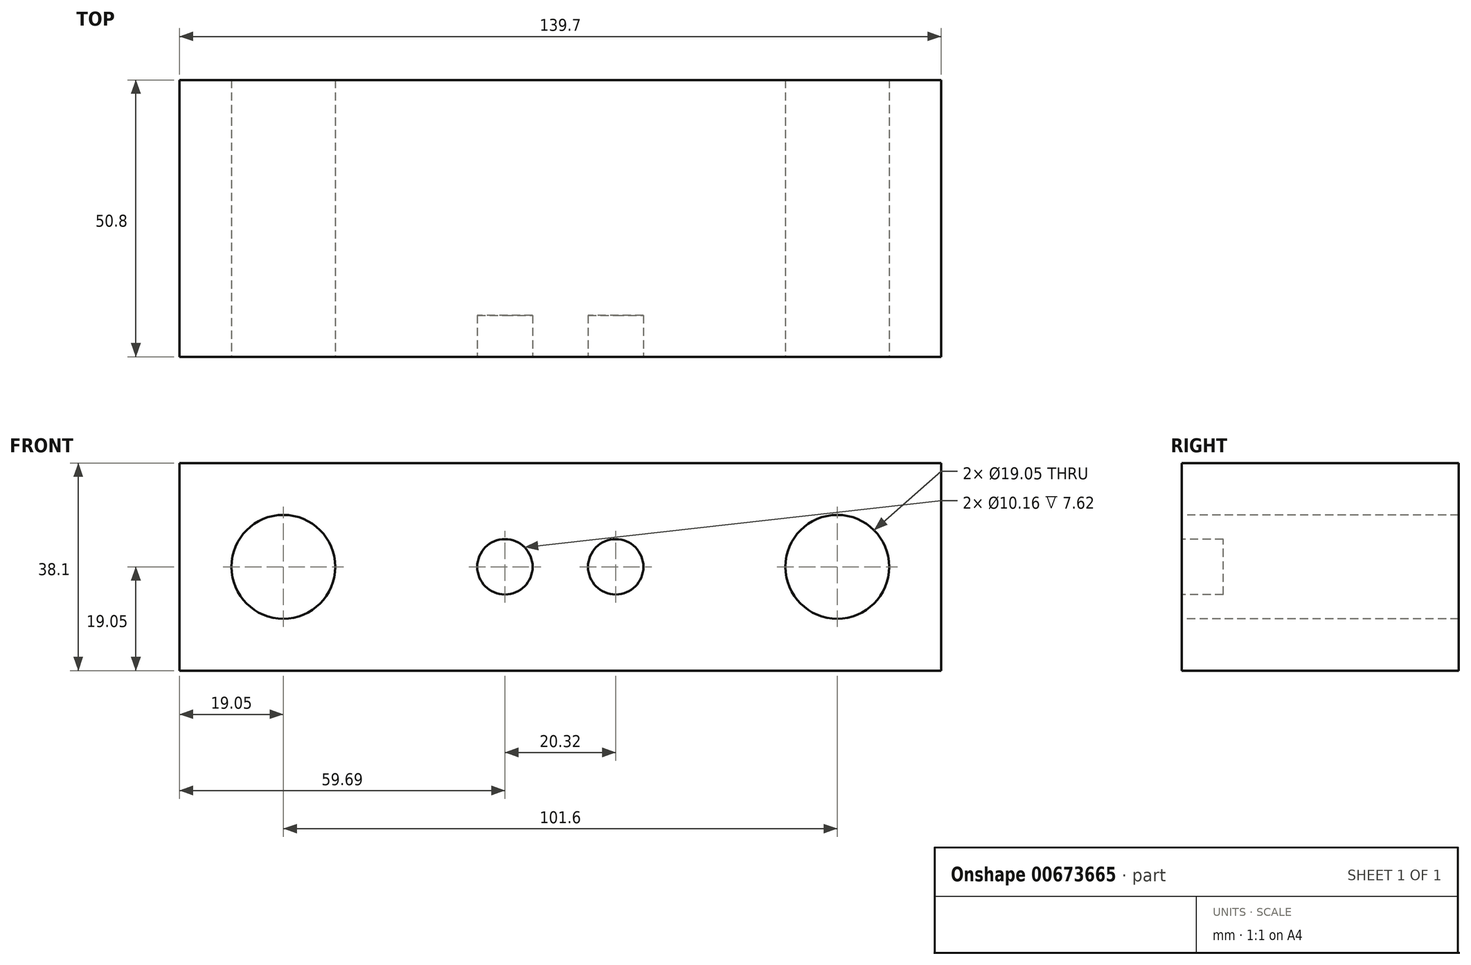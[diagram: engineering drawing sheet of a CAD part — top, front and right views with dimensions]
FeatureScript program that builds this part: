
annotation { "Feature Type Name" : "Feature", "Feature Type Description" : "" }
export const myFeature = defineFeature(function(context is Context, id is Id, definition is map)
    precondition{}
    {
        {
            var Q0;
            Q0=qCreatedBy(makeId("Front.planeOp"),FACE);
            var sketch = newSketch(context, id + "F0", { "sketchPlane" : qUnion([Q0])});
            skLineSegment(sketch, "E0.bottom", {"start": v(69.85, -19.05) * mm, "end": v(-69.85, -19.05) * mm});
            skLineSegment(sketch, "E0.top", {"start": v(69.85, 19.05) * mm, "end": v(-69.85, 19.05) * mm});
            skLineSegment(sketch, "E0.left", {"start": v(69.85, -19.05) * mm, "end": v(69.85, 19.05) * mm});
            skLineSegment(sketch, "E0.right", {"start": v(-69.85, -19.05) * mm, "end": v(-69.85, 19.05) * mm});
            skPoint(sketch, "E0.middle", {"position": v(0, 0) * mm});
            skSolve(sketch);
        }
        {
            var Q0;
            Q0=makeQuery(id+"F0.imprint","IMPRINT",FACE,{"disambiguationData":[TD([[makeQuery(id+"F0.imprint","IMPRINT",EDGE,{"derivedFrom":sQuery(id+"F0.wireOp",EDGE,"E0.bottom")}),-1.0]])]});
            extrude(context, id + "F1", {"entities" : qUnion([Q0]), "endBound" : BoundingType.SYMMETRIC, "depth" : 50.8 * mm, "offsetDistance" : 25.4 * mm});
        }
        {
            var Q0;
            Q0=makeQuery(id+"F1.opExtrude","CAP_FACE",FACE,{"disambiguationData":[OSD([sQuery(id+"F0.wireOp",EDGE,"E0.bottom"),sQuery(id+"F0.wireOp",EDGE,"E0.top"),sQuery(id+"F0.wireOp",EDGE,"E0.left"),sQuery(id+"F0.wireOp",EDGE,"E0.right")])],"isStart":false});
            var sketch = newSketch(context, id + "F2", { "sketchPlane" : qUnion([Q0])});
            skCircle(sketch, "E1", {"center": v(-50.8, 0) * mm, "radius": 9.53 * mm});
            skLineSegment(sketch, "E2", {"start": v(0, 83.1) * mm, "end": v(0, -71.5) * mm});
            skCircle(sketch, "E3.MirrorC", {"center": v(50.8, 0) * mm, "radius": 9.53 * mm});
            skSolve(sketch);
        }
        {
            var Q0;
            Q0 = qSketchRegion(id + "F2", true);
            extrude(context, id + "F3", {"entities" : qUnion([Q0]), "operationType" : NewBodyOperationType.REMOVE, "endBound" : BoundingType.THROUGH_ALL, "oppositeDirection" : true, "depth" : 25.4 * mm, "offsetDistance" : 25.4 * mm});
        }
        {
            var Q0;
            Q0=makeQuery(id+"F1.opExtrude","CAP_FACE",FACE,{"disambiguationData":[OSD([sQuery(id+"F0.wireOp",EDGE,"E0.bottom"),sQuery(id+"F0.wireOp",EDGE,"E0.top"),sQuery(id+"F0.wireOp",EDGE,"E0.left"),sQuery(id+"F0.wireOp",EDGE,"E0.right")])],"isStart":false});
            var sketch = newSketch(context, id + "F4", { "sketchPlane" : qUnion([Q0])});
            skLineSegment(sketch, "E4", {"start": v(0, 28.03) * mm, "end": v(0, -21.69) * mm});
            skCircle(sketch, "E5", {"center": v(-10.16, 0) * mm, "radius": 5.08 * mm});
            skCircle(sketch, "E6.MirrorC", {"center": v(10.16, 0) * mm, "radius": 5.08 * mm});
            skSolve(sketch);
        }
        {
            var Q0;
            Q0 = qSketchRegion(id + "F4", true);
            extrude(context, id + "F5", {"entities" : qUnion([Q0]), "operationType" : NewBodyOperationType.REMOVE, "oppositeDirection" : true, "depth" : 7.62 * mm, "offsetDistance" : 25.4 * mm});
        }
    });
